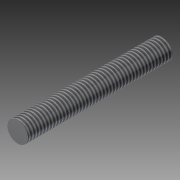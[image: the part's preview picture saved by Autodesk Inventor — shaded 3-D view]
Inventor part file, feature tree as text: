
AUTODESK INVENTOR PART (.ipt)
format: ipt  version: 2014 (Build 180170000, 170)  size: 77,312 bytes
history: native  units: mm
features: extrude x1, thread x1, sketch x1
ambient origin geometry x8: Origin, YZ Plane, XZ Plane, XY Plane, X Axis, Y Axis, Z Axis, Center Point
bodies: Solid1 (feature_tree)
feature tree (3):
  extrude  "Extrusion1"  Depth=35.0mm TaperAngle=0.0deg
  thread  "Thread1"  [1 undecoded]
  sketch  "Sketch1"  dims[d0=5.0mm d1=35.0mm d2=0.0mm d3=10.0mm d4=0.0mm]
note: 1 required parameter value undecoded (feature->parameter linkage not recoverable at this tier; creation-order binding heuristic only, values carry confidence <= 0.55)
